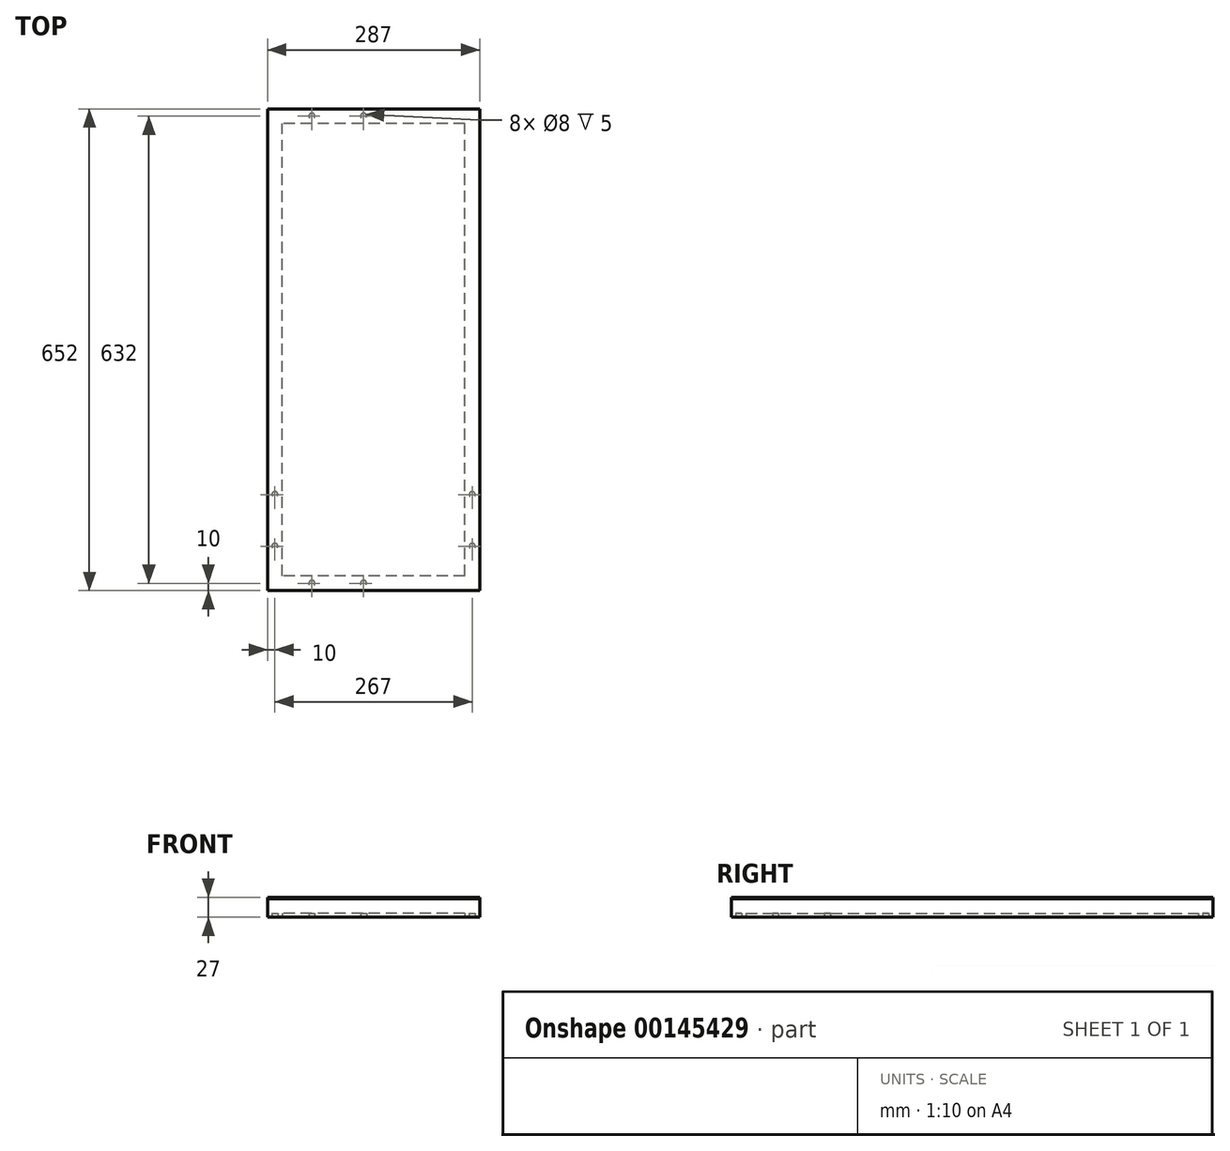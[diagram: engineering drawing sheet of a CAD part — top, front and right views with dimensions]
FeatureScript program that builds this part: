
annotation { "Feature Type Name" : "Feature", "Feature Type Description" : "" }
export const myFeature = defineFeature(function(context is Context, id is Id, definition is map)
    precondition{}
    {
        {
            var Q0;
            Q0=qCreatedBy(makeId("Top.planeOp"),FACE);
            var sketch = newSketch(context, id + "F0", { "sketchPlane" : qUnion([Q0])});
            skLineSegment(sketch, "E0.bottom", {"start": v(143.5, -326) * mm, "end": v(-143.5, -326) * mm});
            skLineSegment(sketch, "E0.top", {"start": v(143.5, 326) * mm, "end": v(-143.5, 326) * mm});
            skLineSegment(sketch, "E0.left", {"start": v(143.5, -326) * mm, "end": v(143.5, 326) * mm});
            skLineSegment(sketch, "E0.right", {"start": v(-143.5, -326) * mm, "end": v(-143.5, 326) * mm});
            skPoint(sketch, "E0.middle", {"position": v(0, 0) * mm});
            skSolve(sketch);
        }
        {
            var Q0;
            Q0=qSketchRegion(id+"F0",true);
            extrude(context, id + "F1", {"entities" : qUnion([Q0]), "depth" : 25 * mm});
        }
        {
            var Q0;
            Q0=makeQuery(id+"F1.opExtrude","CAP_FACE",FACE,{"disambiguationData":[OSD([sQuery(id+"F0.wireOp",EDGE,"E0.bottom"),sQuery(id+"F0.wireOp",EDGE,"E0.top"),sQuery(id+"F0.wireOp",EDGE,"E0.left"),sQuery(id+"F0.wireOp",EDGE,"E0.right")])],"isStart":true});
            shell(context, id + "F2", {"entities" : qUnion([Q0]), "thickness" : 20 * mm});
        }
        {
            var Q0;
            Q0=makeQuery(id+"F1.opExtrude","CAP_FACE",FACE,{"disambiguationData":[OSD([sQuery(id+"F0.wireOp",EDGE,"E0.bottom"),sQuery(id+"F0.wireOp",EDGE,"E0.top"),sQuery(id+"F0.wireOp",EDGE,"E0.left"),sQuery(id+"F0.wireOp",EDGE,"E0.right")])],"isStart":true});
            var sketch = newSketch(context, id + "F3", { "sketchPlane" : qUnion([Q0])});
            skCircle(sketch, "E1", {"center": v(-133.5, 266) * mm, "radius": 4 * mm});
            skCircle(sketch, "E2", {"center": v(-133.5, 196) * mm, "radius": 4 * mm});
            skCircle(sketch, "E3.MirrorC", {"center": v(133.5, 266) * mm, "radius": 4 * mm});
            skCircle(sketch, "E4.MirrorC", {"center": v(133.5, 196) * mm, "radius": 4 * mm});
            skCircle(sketch, "E5", {"center": v(-83.5, 316) * mm, "radius": 4 * mm});
            skCircle(sketch, "E6", {"center": v(-13.5, 316) * mm, "radius": 4 * mm});
            skCircle(sketch, "E7.MirrorC", {"center": v(-13.5, -316) * mm, "radius": 4 * mm});
            skCircle(sketch, "E8.MirrorC", {"center": v(-83.5, -316) * mm, "radius": 4 * mm});
            skSolve(sketch);
        }
        {
            var Q0;
            Q0=qSketchRegion(id+"F3",true);
            extrude(context, id + "F4", {"entities" : qUnion([Q0]), "operationType" : NewBodyOperationType.REMOVE, "oppositeDirection" : true, "depth" : 5 * mm});
        }
        {
            var Q0;
            Q0=makeQuery(id+"F1.opExtrude","CAP_FACE",FACE,{"disambiguationData":[OSD([sQuery(id+"F0.wireOp",EDGE,"E0.bottom"),sQuery(id+"F0.wireOp",EDGE,"E0.top"),sQuery(id+"F0.wireOp",EDGE,"E0.left"),sQuery(id+"F0.wireOp",EDGE,"E0.right")])],"isStart":false});
            var sketch = newSketch(context, id + "F5", { "sketchPlane" : qUnion([Q0])});
            skLineSegment(sketch, "E9.0", {"start": v(143.5, 326) * mm, "end": v(-143.5, 326) * mm});
            skLineSegment(sketch, "E9.1", {"start": v(-143.5, -326) * mm, "end": v(-143.5, 326) * mm});
            skLineSegment(sketch, "E9.2", {"start": v(143.5, -326) * mm, "end": v(-143.5, -326) * mm});
            skLineSegment(sketch, "E9.3", {"start": v(143.5, -326) * mm, "end": v(143.5, 326) * mm});
            skSolve(sketch);
        }
        {
            var Q0;
            Q0 = qSketchRegion(id + "F5", true);
            extrude(context, id + "F6", {"entities" : qUnion([Q0]), "depth" : 2 * mm});
        }
    });
